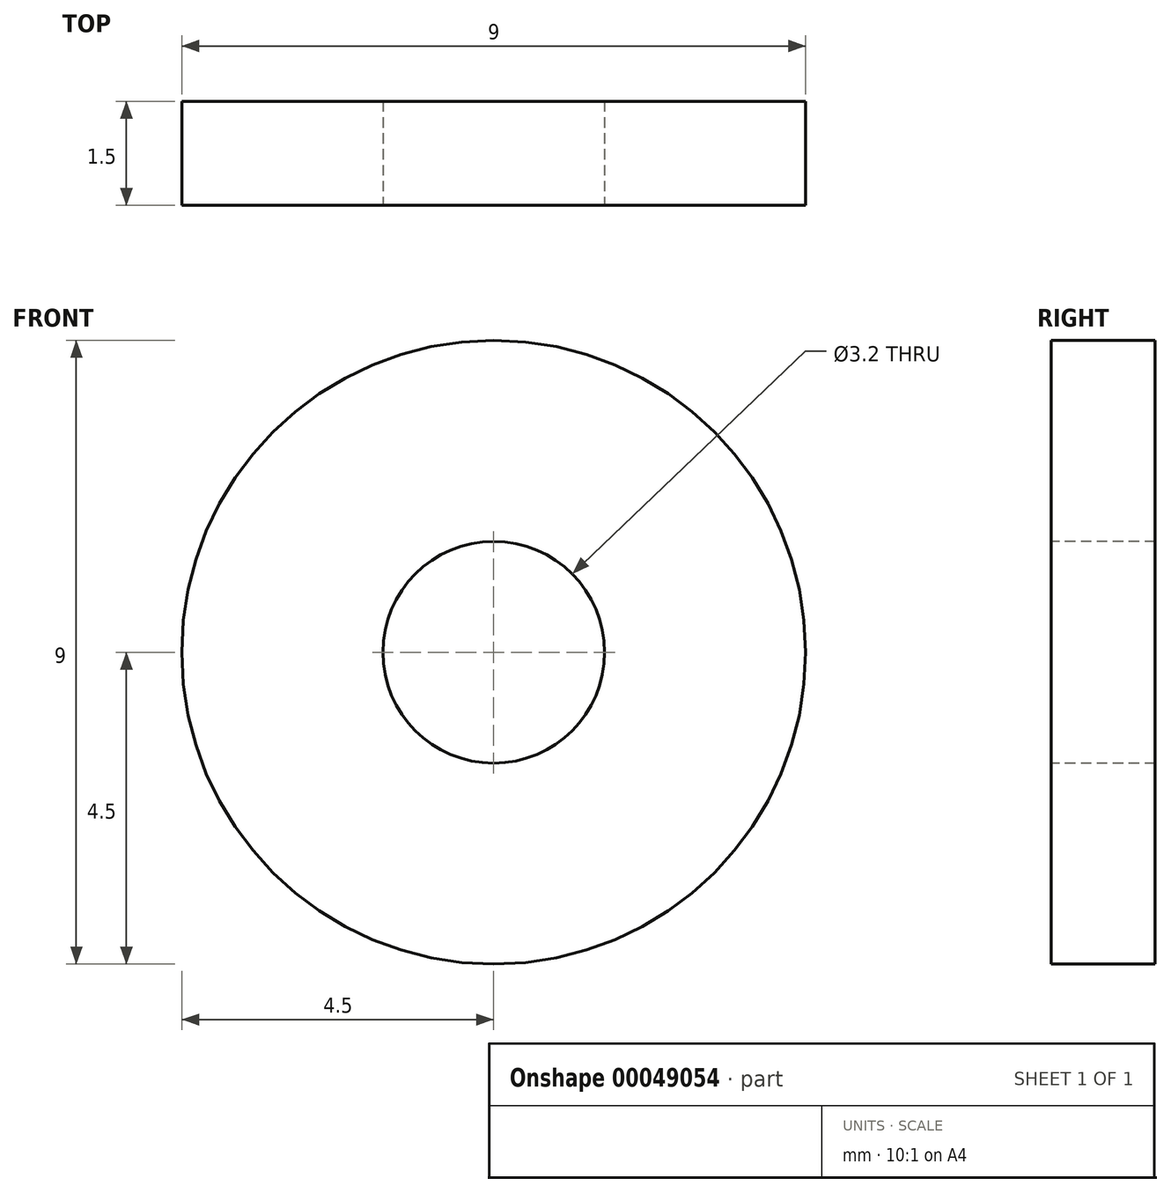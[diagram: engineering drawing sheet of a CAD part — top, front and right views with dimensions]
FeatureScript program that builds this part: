
annotation { "Feature Type Name" : "Feature", "Feature Type Description" : "" }
export const myFeature = defineFeature(function(context is Context, id is Id, definition is map)
    precondition{}
    {
        {
            var Q0;
            Q0=qCreatedBy(makeId("Front.planeOp"),FACE);
            var sketch = newSketch(context, id + "F0", { "sketchPlane" : qUnion([Q0])});
            skCircle(sketch, "E0", {"center": v(0, 0) * mm, "radius": 4.5 * mm});
            skSolve(sketch);
        }
        {
            var Q0;
            Q0 = qSketchRegion(id + "F0", true);
            extrude(context, id + "F1", {"entities" : qUnion([Q0]), "depth" : 1.5 * mm});
        }
        {
            var Q0;
            Q0=makeQuery(id+"F1.opExtrude","CAP_FACE",FACE,{"disambiguationData":[OSD([sQuery(id+"F0.wireOp",EDGE,"E0")])],"isStart":false});
            var sketch = newSketch(context, id + "F2", { "sketchPlane" : qUnion([Q0])});
            skCircle(sketch, "E1", {"center": v(0, 0) * mm, "radius": 1.6 * mm});
            skSolve(sketch);
        }
        {
            var Q0;
            Q0 = qSketchRegion(id + "F2", true);
            extrude(context, id + "F3", {"entities" : qUnion([Q0]), "operationType" : NewBodyOperationType.REMOVE, "endBound" : BoundingType.THROUGH_ALL, "oppositeDirection" : true, "depth" : 25 * mm});
        }
    });
